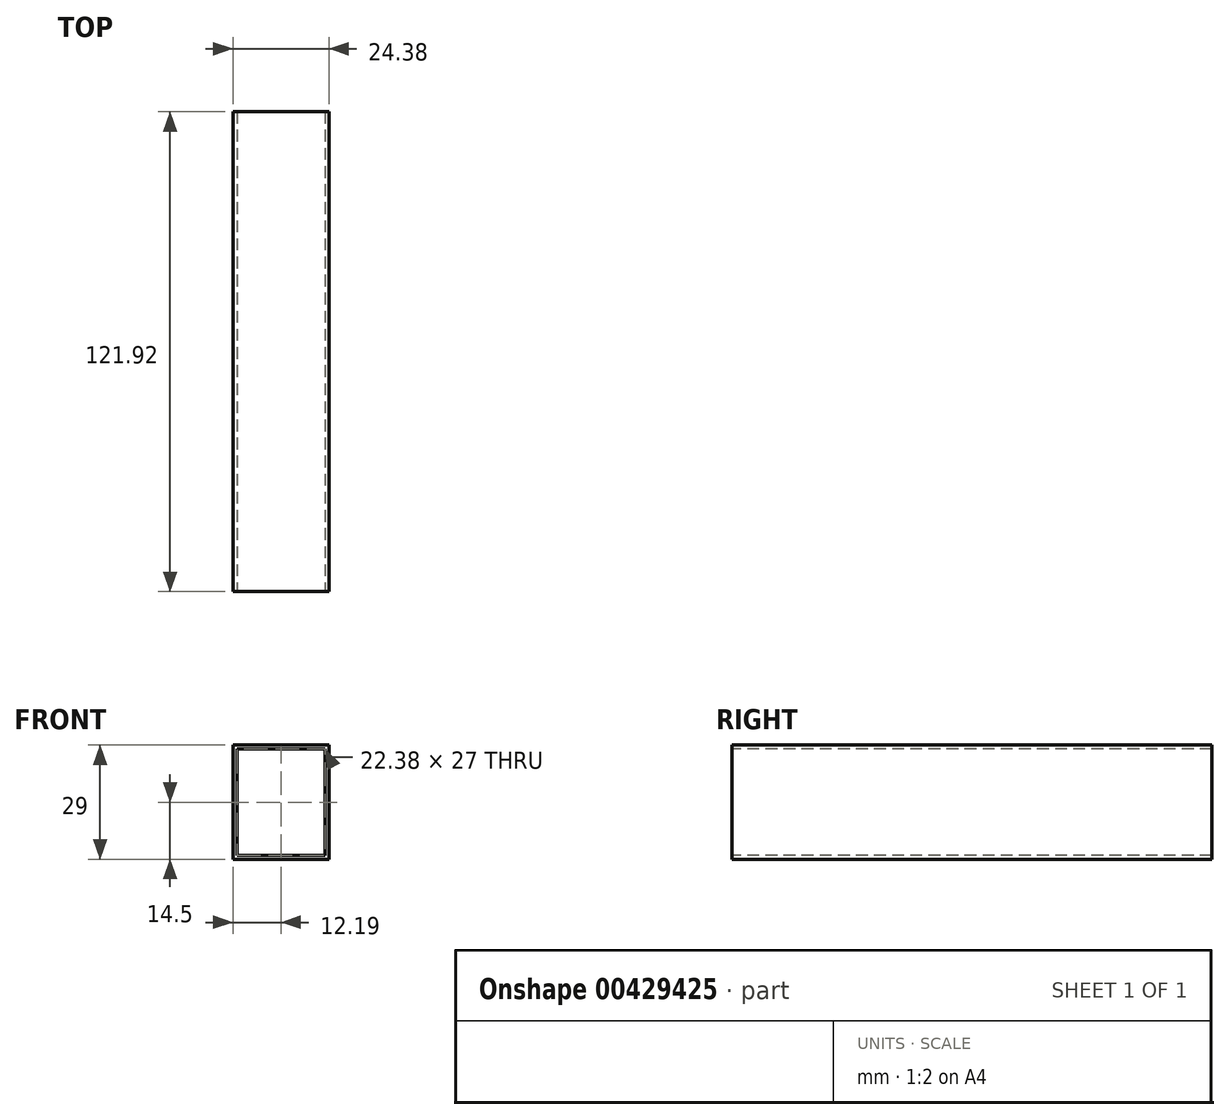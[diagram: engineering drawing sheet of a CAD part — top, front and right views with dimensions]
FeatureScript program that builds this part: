
annotation { "Feature Type Name" : "Feature", "Feature Type Description" : "" }
export const myFeature = defineFeature(function(context is Context, id is Id, definition is map)
    precondition{}
    {
        {
            var Q0;
            Q0=qCreatedBy(makeId("Top.planeOp"),FACE);
            var sketch = newSketch(context, id + "F0", { "sketchPlane" : qUnion([Q0])});
            skLineSegment(sketch, "E0.bottom", {"start": v(12.19, 60.96) * mm, "end": v(-12.2, 60.96) * mm});
            skLineSegment(sketch, "E0.top", {"start": v(12.2, -60.96) * mm, "end": v(-12.19, -60.96) * mm});
            skLineSegment(sketch, "E0.left", {"start": v(12.19, 60.96) * mm, "end": v(12.2, -60.96) * mm});
            skLineSegment(sketch, "E0.right", {"start": v(-12.2, 60.96) * mm, "end": v(-12.19, -60.96) * mm});
            skPoint(sketch, "E0.middle", {"position": v(0, 0) * mm});
            skSolve(sketch);
        }
        {
            var Q0;
            Q0 = qSketchRegion(id + "F0", true);
            extrude(context, id + "F1", {"entities" : qUnion([Q0]), "depth" : 29 * mm});
        }
        {
            var Q0;
            Q0=makeQuery(id+"F1.opExtrude","SWEPT_FACE",FACE,{"disambiguationData":[OSD([sQuery(id+"F0.wireOp",EDGE,"E0.top")])]});
            var sketch = newSketch(context, id + "F2", { "sketchPlane" : qUnion([Q0])});
            skLineSegment(sketch, "E1.bottom", {"start": v(-11.2, 28) * mm, "end": v(11.2, 28) * mm});
            skLineSegment(sketch, "E1.top", {"start": v(-11.2, 1) * mm, "end": v(11.2, 1) * mm});
            skLineSegment(sketch, "E1.left", {"start": v(-11.2, 28) * mm, "end": v(-11.2, 1) * mm});
            skLineSegment(sketch, "E1.right", {"start": v(11.2, 28) * mm, "end": v(11.2, 1) * mm});
            skPoint(sketch, "E1.middle", {"position": v(0, 14.5) * mm});
            skSolve(sketch);
        }
        {
            var Q0;
            Q0 = qSketchRegion(id + "F2", true);
            extrude(context, id + "F3", {"entities" : qUnion([Q0]), "operationType" : NewBodyOperationType.REMOVE, "endBound" : BoundingType.THROUGH_ALL, "oppositeDirection" : true, "depth" : 25 * mm});
        }
    });
